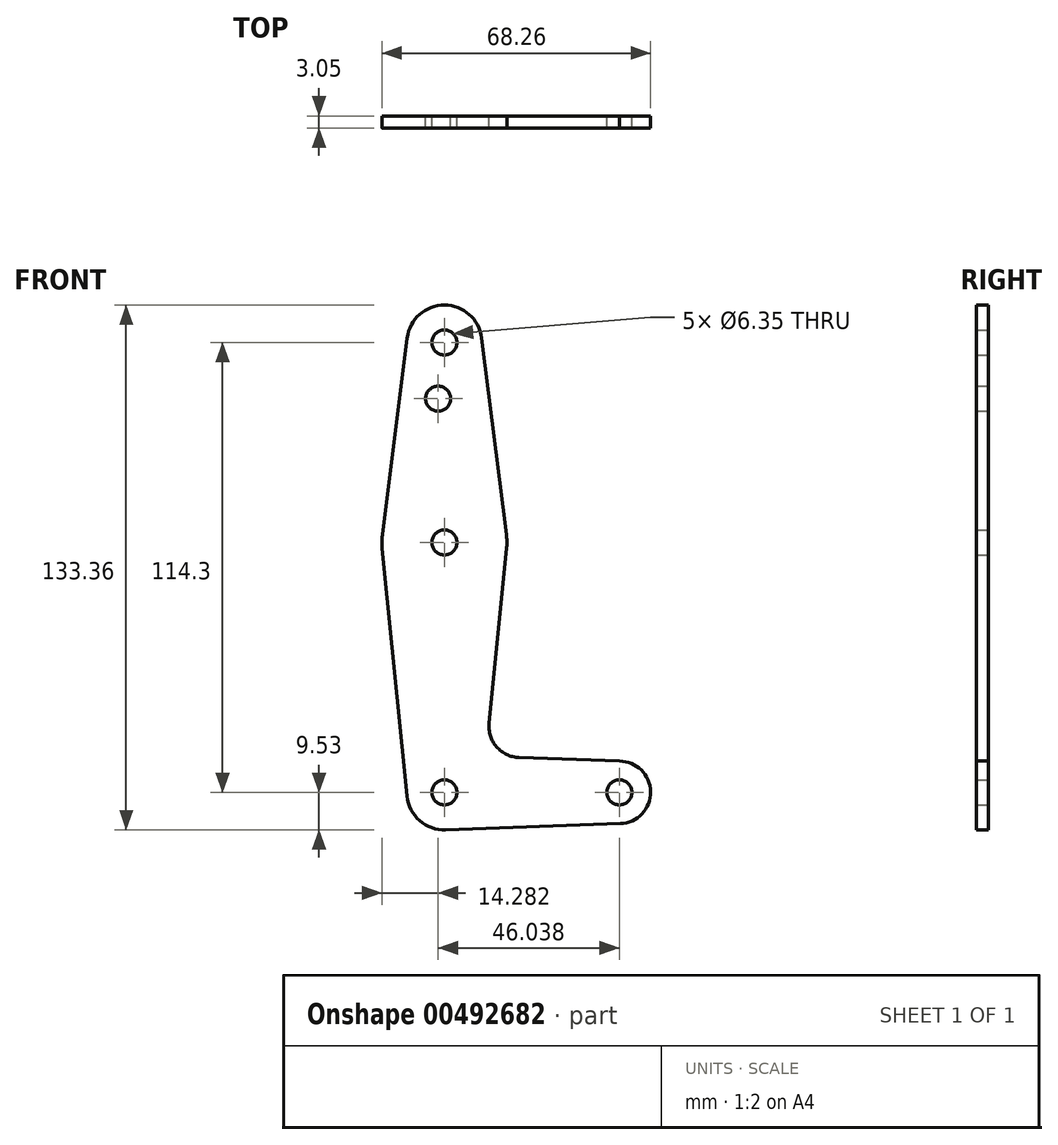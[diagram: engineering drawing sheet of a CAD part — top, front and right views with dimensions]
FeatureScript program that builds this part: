
annotation { "Feature Type Name" : "Feature", "Feature Type Description" : "" }
export const myFeature = defineFeature(function(context is Context, id is Id, definition is map)
    precondition{}
    {
        {
            var Q0;
            Q0=qCreatedBy(makeId("Front.planeOp"),FACE);
            var sketch = newSketch(context, id + "F0", { "sketchPlane" : qUnion([Q0])});
            skLineSegment(sketch, "E0", {"start": v(0, 0) * mm, "end": v(0, 114.3) * mm, "construction": true});
            skLineSegment(sketch, "E1", {"start": v(0, 0) * mm, "end": v(44.45, 0) * mm, "construction": true});
            skCircle(sketch, "E2", {"center": v(0, 0) * mm, "radius": 9.53 * mm});
            skCircle(sketch, "E3", {"center": v(0, 63.5) * mm, "radius": 15.88 * mm});
            skCircle(sketch, "E4", {"center": v(44.45, 0) * mm, "radius": 7.94 * mm});
            skLineSegment(sketch, "E5", {"start": v(15.8, 61.91) * mm, "end": v(11.34, 17.6) * mm});
            skLineSegment(sketch, "E6", {"start": v(0.34, -9.52) * mm, "end": v(44.73, -7.93) * mm});
            skLineSegment(sketch, "E7", {"start": v(18.97, 8.85) * mm, "end": v(44.45, 7.94) * mm});
            skLineSegment(sketch, "E8", {"start": v(-15.8, 61.91) * mm, "end": v(-9.48, -0.95) * mm});
            skCircle(sketch, "E9", {"center": v(0, 114.3) * mm, "radius": 9.53 * mm});
            skLineSegment(sketch, "E10", {"start": v(-9.45, 115.5) * mm, "end": v(-15.75, 65.48) * mm});
            skLineSegment(sketch, "E11", {"start": v(9.45, 115.5) * mm, "end": v(15.75, 65.48) * mm});
            skCircle(sketch, "E12", {"center": v(0, 114.3) * mm, "radius": 3.18 * mm});
            skCircle(sketch, "E13", {"center": v(0, 63.5) * mm, "radius": 3.18 * mm});
            skCircle(sketch, "E14", {"center": v(-1.59, 100.03) * mm, "radius": 3.18 * mm});
            skCircle(sketch, "E15", {"center": v(0, 0) * mm, "radius": 3.18 * mm});
            skCircle(sketch, "E16", {"center": v(44.45, 0) * mm, "radius": 3.18 * mm});
            skArc(sketch, "E17.filletArc", {"start": v(11.34, 17.6) * mm, "mid": v(13.26, 11.57) * mm, "end": v(18.97, 8.85) * mm});
            skSolve(sketch);
        }
        {
            var Q0;
            {var subQ0=sQuery(id+"F0.wireOp",EDGE,"E5");Q0=makeQuery(id+"F0.imprint","IMPRINT",FACE,{"disambiguationData":[TD([[makeQuery(id+"F0.imprint","IMPRINT",EDGE,{"derivedFrom":subQ0}),-1.0]])]});}
            var Q1;
            Q1=makeQuery(id+"F0.imprint","IMPRINT",FACE,{"disambiguationData":[TD([[makeQuery(id+"F0.imprint","IMPRINT",EDGE,{"derivedFrom":sQuery(id+"F0.wireOp",EDGE,"E15")}),-1.0]])]});
            var Q2;
            Q2=makeQuery(id+"F0.imprint","IMPRINT",FACE,{"disambiguationData":[TD([[makeQuery(id+"F0.imprint","IMPRINT",EDGE,{"derivedFrom":sQuery(id+"F0.wireOp",EDGE,"E16")}),-1.0]])]});
            var Q3;
            Q3=makeQuery(id+"F0.imprint","IMPRINT",FACE,{"disambiguationData":[TD([[makeQuery(id+"F0.imprint","IMPRINT",EDGE,{"derivedFrom":sQuery(id+"F0.wireOp",EDGE,"E12")}),-1.0]])]});
            var Q4;
            {var subQ1=sQuery(id+"F0.wireOp",EDGE,"E10");Q4=makeQuery(id+"F0.imprint","IMPRINT",FACE,{"disambiguationData":[TD([[makeQuery(id+"F0.imprint","IMPRINT",EDGE,{"derivedFrom":subQ1}),1.0]])]});}
            var Q5;
            Q5=makeQuery(id+"F0.imprint","IMPRINT",FACE,{"disambiguationData":[TD([[makeQuery(id+"F0.imprint","IMPRINT",EDGE,{"derivedFrom":sQuery(id+"F0.wireOp",EDGE,"E13")}),-1.0]])]});
            extrude(context, id + "F1", {"entities" : qUnion([Q0, Q1, Q2, Q3, Q4, Q5]), "depth" : 3.05 * mm});
        }
    });
